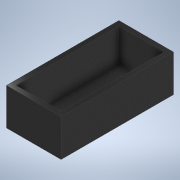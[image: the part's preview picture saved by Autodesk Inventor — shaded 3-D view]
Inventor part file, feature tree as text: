
AUTODESK INVENTOR PART (.ipt)
format: ipt  version: 2022.2 (Build 262287010, 287A)  size: 238,592 bytes
history: native  units: in
note: dims shown in document units (in); Inventor stores cm internally (conversion verified against a paired STEP export)
features: extrude x10, sketch x6, other x1
ambient origin geometry x8: Origin, YZ Plane, XZ Plane, XY Plane, X Axis, Y Axis, Z Axis, Center Point
bodies: Body1 (feature_tree)
feature tree (17):
  other  "Sólido1"
  sketch  "Boceto1"  dims[d0=6.6929in d1=13.7795in]
  extrude  "Extrusión1"  Depth=13.7795in
  extrude  "Extrusión2"  Depth=3.937in TaperAngle=0.0deg
  extrude  "Extrusión3"  Depth=3.937in
  sketch  "Boceto2"  dims[d2=0.5906in d3=3.937in d4=0.0in]
  extrude  "Extrusión4"  Depth=0.3937in
  extrude  "Extrusión5"  Depth=0.5906in
  extrude  "Extrusión6"  TaperAngle=0.0deg  [1 undecoded]
  sketch  "Boceto3"  dims[d5=3.937in d6=0.0in d7=3.937in]
  extrude  "Extrusión12"  Depth=3.937in TaperAngle=0.0deg
  extrude  "Extrusión13"  Depth=3.937in TaperAngle=0.0deg
  sketch  "Boceto8"  dims[d8=5.7406in d9=0.3937in]
  sketch  "Boceto9"  dims[d10=0.5906in d11=0.0in d12=1.122in]
  extrude  "Extrusión14"  Depth=0.3555in
  sketch  "Boceto10"  dims[d13=1.122in d16=0.0in d17=0.0in d18=3.937in d19=0.0in d20=3.937in d21=0.0in d46=0.3555in d47=0.3583in d48=0.5102in d54=3.3465in d55=0.2756in d58=0.1969in d59=0.0in d60=0.0in d61=0.0in d62=1.1811in d63=1.1811in d66=3.937in d67=3.5114in d68=2.7559in d69=4.6185in d70=3.5815in d71=6.3524in d72=2.7559in d73=0.2965in d74=3.6406in d80=3.937in d83=1.5748in d86=0.2953in d87=0.2953in d88=0.7874in d89=0.5906in d90=0.1969in d91=0.0in d92=7.874in d93=90.0deg d94=0.2953in d95=1.0039in d96=0.1969in d97=0.1969in d98=0.7874in d99=1.5748in d100=0.1969in d101=0.0in]
  extrude  "Extrusión15"  Depth=0.3583in
note: 1 required parameter value undecoded (feature->parameter linkage not recoverable at this tier; creation-order binding heuristic only, values carry confidence <= 0.55)
